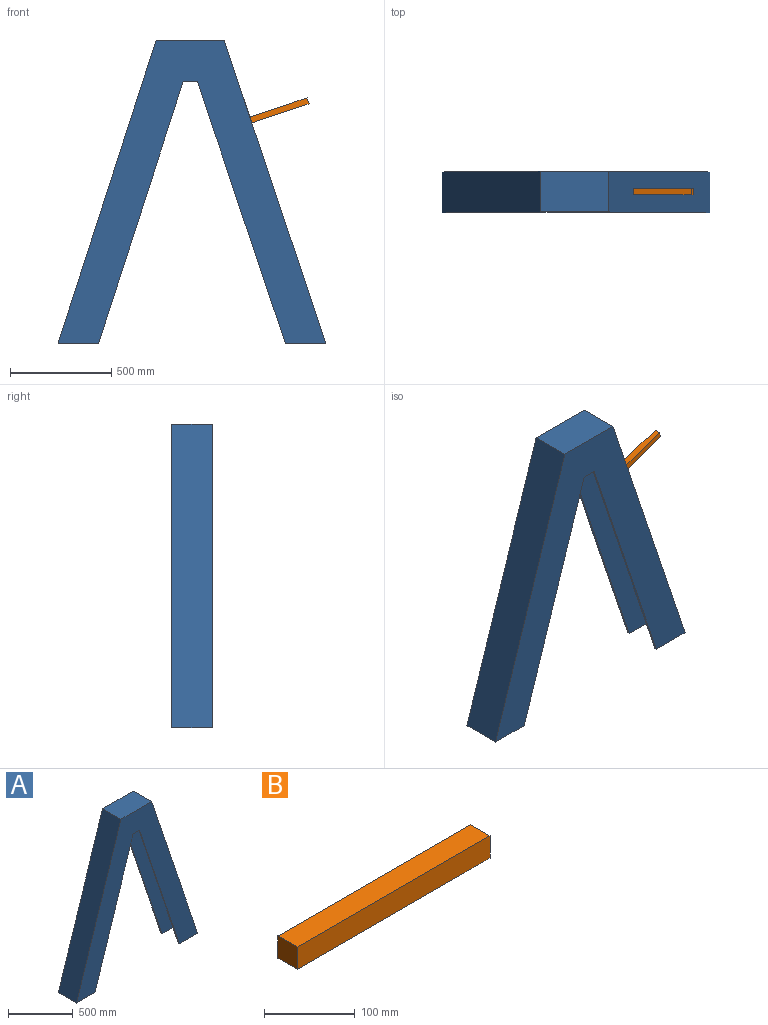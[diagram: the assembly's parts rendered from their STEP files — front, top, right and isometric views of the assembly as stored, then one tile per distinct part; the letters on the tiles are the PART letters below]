
ASSEMBLY  parts=2 mates=1
PART A: 23 faces, bbox 1322.7x200x1497.4 mm
  f0: plane 1497.4x503.18mm, normal (0.95,0,0.32), area 315036.2mm2, adj f4,f7,f11,f12,f18,f19,f20,f21
  f1: plane 70.57x10mm, normal (0,0,-1), area 705.7mm2, adj f2,f5,f12,f17
  f2: plane 1292.93x417.68mm, normal (0.95,0,-0.31), area 13587.2mm2, adj f1,f3,f12,f17
  f3: plane 200x200mm, normal (0,0,-1), area 5891.6mm2, adj f2,f8,f9,f11,f12,f15,f16,f17
  f4: plane 200x200mm, normal (0,0,-1), area 5898.9mm2, adj f0,f5,f6,f11,f12,f13,f16,f17
  f5: plane 1292.93x434.47mm, normal (-0.95,0,-0.32), area 13639.7mm2, adj f1,f4,f12,f17
  f6: plane 1292.93x434.47mm, normal (-0.95,0,-0.32), area 13639.7mm2, adj f4,f10,f11,f16
  f7: plane 335.81x200mm, normal (0,0,1), area 67161.3mm2, adj f0,f8,f11,f12
  f8: plane 1497.4x483.74mm, normal (-0.95,0,0.31), area 314718.9mm2, adj f3,f7,f11,f12
  f9: plane 1292.93x417.68mm, normal (0.95,0,-0.31), area 13587.2mm2, adj f3,f10,f11,f16
  f10: plane 70.57x10mm, normal (0,0,-1), area 705.7mm2, adj f6,f9,f11,f16
  f11: plane 1497.4x1322.73mm, normal (0,-1,0), area 599610.9mm2, adj f0,f3,f4,f6,f7,f8,f9,f10
  f12: plane 1497.4x1322.73mm, normal (0,1,0), area 599610.9mm2, adj f0,f1,f2,f3,f4,f5,f7,f8
  f13: plane 1487.4x499.82mm, normal (-0.95,0,-0.32), area 282443.7mm2, adj f4,f14,f16,f17
  f14: plane 321.34x180mm, normal (0,0,-1), area 57841mm2, adj f13,f15,f16,f17
  f15: plane 1487.4x480.51mm, normal (0.95,0,-0.31), area 281355.4mm2, adj f3,f14,f16,f17
  f16: plane 1487.4x1301.67mm, normal (0,1,0), area 564897.7mm2, adj f3,f4,f6,f9,f10,f13,f14,f15
  f17: plane 1487.4x1301.67mm, normal (0,-1,0), area 564897.7mm2, adj f1,f2,f3,f4,f5,f13,f14,f15
  f18: plane 30x1.9mm, normal (0.32,0,-0.95), area 60mm2, adj f0,f19,f21,f22
  f19: plane 29.07x11.45mm, normal (0,1,0), area 60mm2, adj f0,f18,f20,f22
  f20: plane 30x1.9mm, normal (-0.32,0,0.95), area 60mm2, adj f0,f19,f21,f22
  f21: plane 29.07x11.45mm, normal (0,-1,0), area 60mm2, adj f0,f18,f20,f22
  f22: plane 30x28.44mm, normal (0.95,0,0.32), area 900mm2, adj f18,f19,f20,f21
PART B: 6 faces, bbox 300x30x30 mm
  f0: plane 300x30mm, normal (0,0,1), area 9000mm2, adj f1,f3,f4,f5
  f1: plane 300x30mm, normal (0,-1,0), area 9000mm2, adj f0,f2,f4,f5
  f2: plane 300x30mm, normal (0,0,-1), area 9000mm2, adj f1,f3,f4,f5
  f3: plane 300x30mm, normal (0,1,0), area 9000mm2, adj f0,f2,f4,f5
  f4: plane 30x30mm, normal (1,0,0), area 900mm2, adj f0,f1,f2,f3
  f5: plane 30x30mm, normal (-1,0,0), area 900mm2, adj f0,f1,f2,f3
PLACE A t=(-12.76,98.81,-192.77)mm fixed
PLACE B rot(axis=(0,-1,0),18.6deg) t=(293.35,0.49,330.66)mm
MATE fastened A.f22 <-> B.f5  axis (0.95,0,0.32) through (284.81,-1.19,356.06)mm
